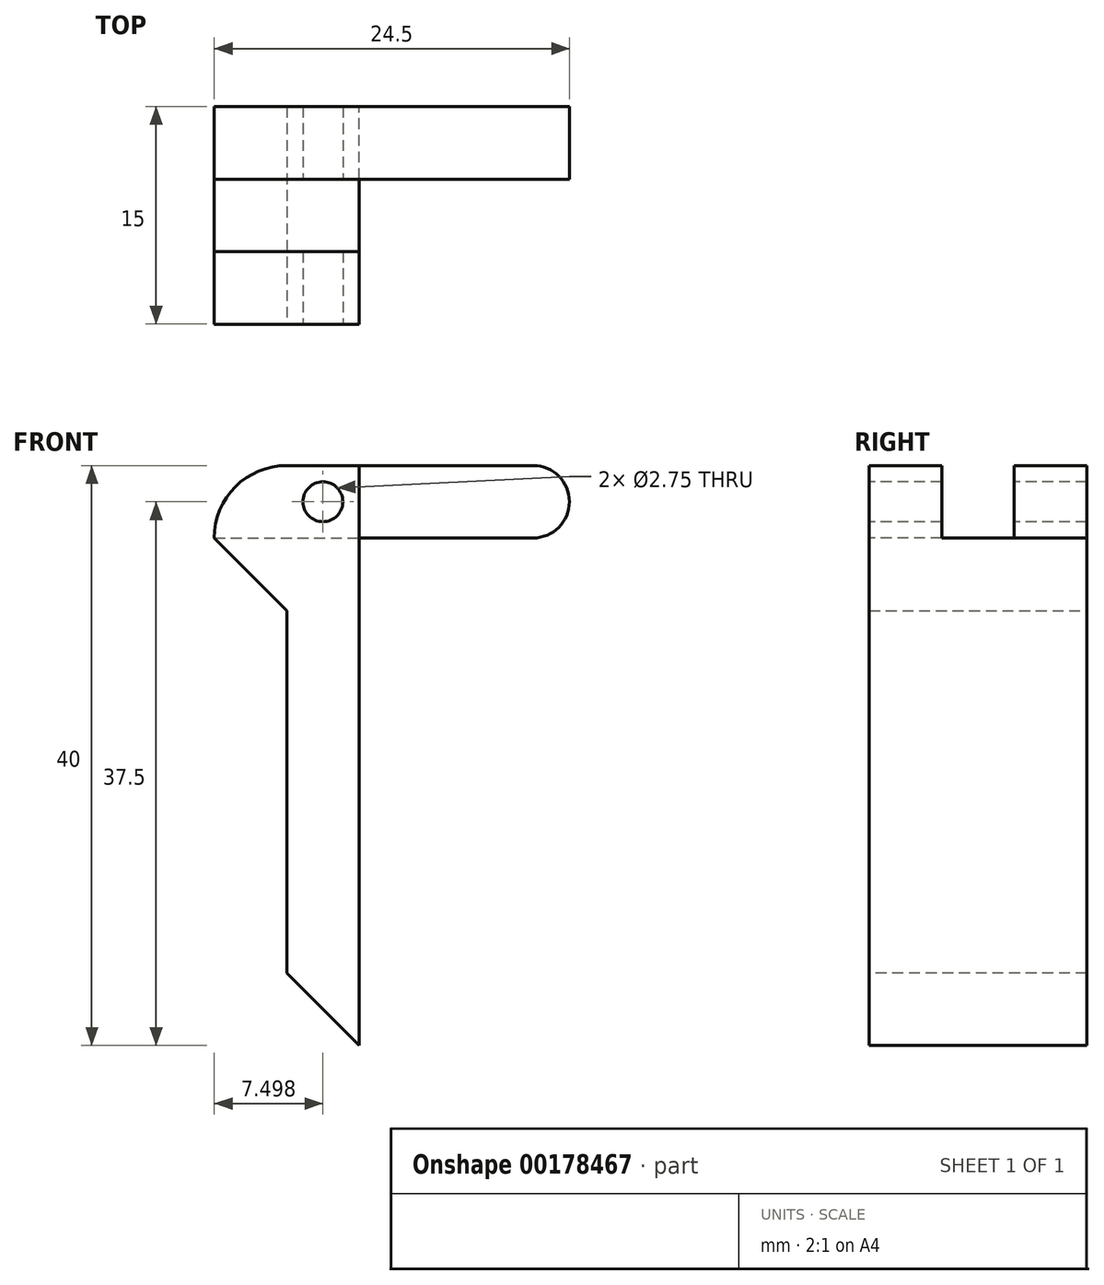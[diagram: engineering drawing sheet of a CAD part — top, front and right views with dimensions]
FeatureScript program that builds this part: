
annotation { "Feature Type Name" : "Feature", "Feature Type Description" : "" }
export const myFeature = defineFeature(function(context is Context, id is Id, definition is map)
    precondition{}
    {
        {
            var Q0;
            Q0=qCreatedBy(makeId("Top.planeOp"),FACE);
            var sketch = newSketch(context, id + "F0", { "sketchPlane" : qUnion([Q0])});
            skLineSegment(sketch, "E0.bottom", {"start": v(-31.67, -29) * mm, "end": v(-21.67, -29) * mm});
            skLineSegment(sketch, "E0.top", {"start": v(-31.67, -14) * mm, "end": v(-21.67, -14) * mm});
            skLineSegment(sketch, "E0.left", {"start": v(-31.67, -29) * mm, "end": v(-31.67, -14) * mm});
            skLineSegment(sketch, "E0.right", {"start": v(-21.67, -29) * mm, "end": v(-21.67, -14) * mm});
            skSolve(sketch);
        }
        {
            var Q0;
            Q0 = qSketchRegion(id + "F0", true);
            extrude(context, id + "F1", {"entities" : qUnion([Q0]), "depth" : 5 * mm});
        }
        {
            var Q0;
            Q0=makeQuery(id+"F1.opExtrude","CAP_FACE",FACE,{"disambiguationData":[OSD([sQuery(id+"F0.wireOp",EDGE,"E0.bottom"),sQuery(id+"F0.wireOp",EDGE,"E0.top"),sQuery(id+"F0.wireOp",EDGE,"E0.left"),sQuery(id+"F0.wireOp",EDGE,"E0.right")])],"isStart":false});
            extrude(context, id + "F2", {"entities" : qUnion([Q0]), "operationType" : NewBodyOperationType.ADD, "depth" : 5 * mm});
        }
        {
            var Q0;
            {var subQ0=sQuery(id+"F0.wireOp",EDGE,"E0.bottom");Q0=makeQuery(id+"F2.boolean.opBoolean","MERGE",FACE,{"derivedFrom":[makeQuery(id+"F1.opExtrude","SWEPT_FACE",FACE,{"disambiguationData":[OSD([subQ0])]}),makeQuery(id+"F2.opExtrude","SWEPT_FACE",FACE,{"disambiguationData":[OSD([subQ0])]})]});}
            var sketch = newSketch(context, id + "F3", { "sketchPlane" : qUnion([Q0])});
            skLineSegment(sketch, "E1", {"start": v(-21.67, 10) * mm, "end": v(-21.67, 7.5) * mm});
            skLineSegment(sketch, "E2", {"start": v(-21.67, 7.5) * mm, "end": v(-24.17, 7.5) * mm});
            skCircle(sketch, "E3", {"center": v(-24.17, 7.5) * mm, "radius": 1.38 * mm});
            skSolve(sketch);
        }
        {
            var Q0;
            Q0 = qSketchRegion(id + "F3", true);
            extrude(context, id + "F4", {"entities" : qUnion([Q0]), "operationType" : NewBodyOperationType.REMOVE, "endBound" : BoundingType.THROUGH_ALL, "oppositeDirection" : true, "depth" : 25 * mm});
        }
        {
            var Q0;
            {var subQ0=sQuery(id+"F0.wireOp",EDGE,"E0.right");Q0=makeQuery(id+"F2.boolean.opBoolean","MERGE",FACE,{"derivedFrom":[makeQuery(id+"F1.opExtrude","SWEPT_FACE",FACE,{"disambiguationData":[OSD([subQ0])]}),makeQuery(id+"F2.opExtrude","SWEPT_FACE",FACE,{"disambiguationData":[OSD([subQ0])]})]});}
            var sketch = newSketch(context, id + "F5", { "sketchPlane" : qUnion([Q0])});
            skLineSegment(sketch, "E4.bottom", {"start": v(-14, 10) * mm, "end": v(-19, 10) * mm});
            skLineSegment(sketch, "E4.top", {"start": v(-14, 5) * mm, "end": v(-19, 5) * mm});
            skLineSegment(sketch, "E4.left", {"start": v(-14, 10) * mm, "end": v(-14, 5) * mm});
            skLineSegment(sketch, "E4.right", {"start": v(-19, 10) * mm, "end": v(-19, 5) * mm});
            skLineSegment(sketch, "E5.bottom", {"start": v(-19, 10) * mm, "end": v(-24, 10) * mm});
            skLineSegment(sketch, "E5.top", {"start": v(-19, 5) * mm, "end": v(-24, 5) * mm});
            skLineSegment(sketch, "E5.right", {"start": v(-24, 10) * mm, "end": v(-24, 5) * mm});
            skSolve(sketch);
        }
        {
            var Q0;
            Q0=makeQuery(id+"F5.imprint","IMPRINT",FACE,{"disambiguationData":[TD([[makeQuery(id+"F5.imprint","IMPRINT",EDGE,{"derivedFrom":sQuery(id+"F5.wireOp",EDGE,"E5.bottom")}),-1.0]])]});
            extrude(context, id + "F6", {"entities" : qUnion([Q0]), "operationType" : NewBodyOperationType.REMOVE, "endBound" : BoundingType.THROUGH_ALL, "oppositeDirection" : true, "depth" : 25 * mm});
        }
        {
            var Q0;
            {var subQ0=sQuery(id+"F0.wireOp",EDGE,"E0.right");Q0=makeQuery(id+"F2.boolean.opBoolean","MERGE",FACE,{"derivedFrom":[makeQuery(id+"F1.opExtrude","SWEPT_FACE",FACE,{"disambiguationData":[OSD([subQ0])]}),makeQuery(id+"F2.opExtrude","SWEPT_FACE",FACE,{"disambiguationData":[OSD([subQ0])]})]});}
            var sketch = newSketch(context, id + "F7", { "sketchPlane" : qUnion([Q0])});
            skLineSegment(sketch, "E6.bottom", {"start": v(-19, 5) * mm, "end": v(-14, 5) * mm});
            skLineSegment(sketch, "E6.top", {"start": v(-19, 10) * mm, "end": v(-14, 10) * mm});
            skLineSegment(sketch, "E6.left", {"start": v(-19, 5) * mm, "end": v(-19, 10) * mm});
            skLineSegment(sketch, "E6.right", {"start": v(-14, 5) * mm, "end": v(-14, 10) * mm});
            skSolve(sketch);
        }
        {
            var Q0;
            Q0 = qSketchRegion(id + "F7", true);
            extrude(context, id + "F8", {"entities" : qUnion([Q0]), "operationType" : NewBodyOperationType.ADD, "depth" : 14.5 * mm});
        }
        {
            var Q0;
            Q0=makeQuery(id+"F1.opExtrude","CAP_FACE",FACE,{"disambiguationData":[OSD([sQuery(id+"F0.wireOp",EDGE,"E0.bottom"),sQuery(id+"F0.wireOp",EDGE,"E0.top"),sQuery(id+"F0.wireOp",EDGE,"E0.left"),sQuery(id+"F0.wireOp",EDGE,"E0.right")])],"isStart":true});
            var sketch = newSketch(context, id + "F9", { "sketchPlane" : qUnion([Q0])});
            skLineSegment(sketch, "E7.bottom", {"start": v(-21.67, 29) * mm, "end": v(-26.67, 29) * mm});
            skLineSegment(sketch, "E7.top", {"start": v(-21.67, 14) * mm, "end": v(-26.67, 14) * mm});
            skLineSegment(sketch, "E7.left", {"start": v(-21.67, 29) * mm, "end": v(-21.67, 14) * mm});
            skLineSegment(sketch, "E7.right", {"start": v(-26.67, 29) * mm, "end": v(-26.67, 14) * mm});
            skSolve(sketch);
        }
        {
            var Q0;
            Q0 = qSketchRegion(id + "F9", true);
            extrude(context, id + "F10", {"entities" : qUnion([Q0]), "operationType" : NewBodyOperationType.ADD, "depth" : 30 * mm});
        }
        {
            var Q0;
            Q0=makeQuery(id+"F8.opExtrude","CAP_EDGE",EDGE,{"disambiguationData":[OSD([sQuery(id+"F7.wireOp",EDGE,"E6.top")])],"isStart":false});
            var Q1;
            Q1=makeQuery(id+"F8.opExtrude","CAP_EDGE",EDGE,{"disambiguationData":[OSD([sQuery(id+"F7.wireOp",EDGE,"E6.bottom")])],"isStart":false});
            fillet(context, id + "F11", {"entities" : qUnion([Q0, Q1]), "radius" : 2.5 * mm, "tangentPropagation" : true, "allowEdgeOverflow" : false});
        }
        {
            var Q0;
            Q0=makeQuery(id+"F1.opExtrude","CAP_EDGE",EDGE,{"disambiguationData":[OSD([sQuery(id+"F0.wireOp",EDGE,"E0.left")])],"isStart":true});
            chamfer(context, id + "F12", {"entities" : qUnion([Q0]), "width" : 5 * mm, "tangentPropagation" : true});
        }
        {
            var Q0;
            {var subQ0=sQuery(id+"F0.wireOp",EDGE,"E0.left");var subQ1=sQuery(id+"F0.wireOp",EDGE,"E0.top");Q0=makeQuery(id+"F6.boolean.opBoolean","SPLIT",EDGE,{"disambiguationData":[TD([makeQuery(id+"F1.opExtrude","SWEPT_FACE",FACE,{"disambiguationData":[OSD([subQ1])]})])],"derivedFrom":makeQuery(id+"F2.opExtrude","CAP_EDGE",EDGE,{"disambiguationData":[OSD([subQ0])],"isStart":false})});}
            var Q1;
            {var subQ0=sQuery(id+"F0.wireOp",EDGE,"E0.left");var subQ1=sQuery(id+"F0.wireOp",EDGE,"E0.bottom");Q1=makeQuery(id+"F6.boolean.opBoolean","SPLIT",EDGE,{"disambiguationData":[TD([makeQuery(id+"F1.opExtrude","SWEPT_FACE",FACE,{"disambiguationData":[OSD([subQ1])]})])],"derivedFrom":makeQuery(id+"F2.opExtrude","CAP_EDGE",EDGE,{"disambiguationData":[OSD([subQ0])],"isStart":false})});}
            fillet(context, id + "F13", {"entities" : qUnion([Q0, Q1]), "radius" : 5 * mm, "tangentPropagation" : true, "allowEdgeOverflow" : false});
        }
        {
            var Q0;
            Q0=makeQuery(id+"F10.opExtrude","CAP_EDGE",EDGE,{"disambiguationData":[OSD([sQuery(id+"F9.wireOp",EDGE,"E7.right")])],"isStart":false});
            chamfer(context, id + "F14", {"entities" : qUnion([Q0]), "width" : 5 * mm, "tangentPropagation" : true});
        }
        {
            var Q0;
            Q0=makeQuery(id+"F8.boolean.opBoolean","MERGE",FACE,{"derivedFrom":[makeQuery(id+"F6.boolean.opBoolean","COPY",FACE,{"derivedFrom":makeQuery(id+"F6.opExtrude","SWEPT_FACE",FACE,{"disambiguationData":[OSD([sQuery(id+"F5.wireOp",EDGE,"E4.right")])]})}),makeQuery(id+"F8.opExtrude","SWEPT_FACE",FACE,{"disambiguationData":[OSD([sQuery(id+"F7.wireOp",EDGE,"E6.left")])]})]});
            var sketch = newSketch(context, id + "F15", { "sketchPlane" : qUnion([Q0])});
            skPoint(sketch, "E8.endSnap0", {"position": v(-7.17, 7.5) * mm});
            skSolve(sketch);
        }
    });
